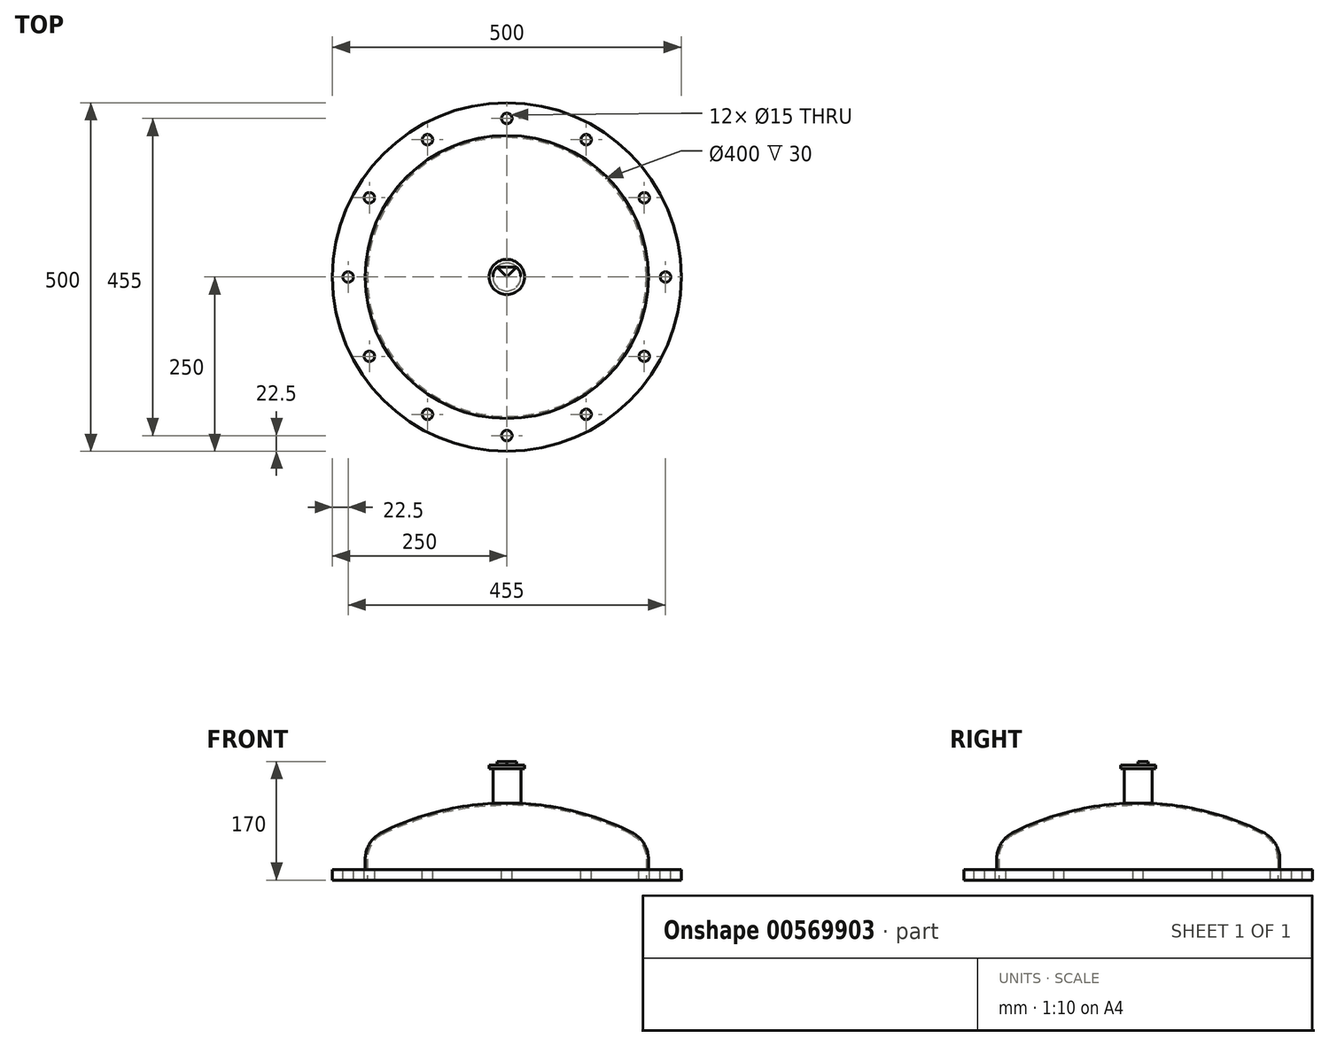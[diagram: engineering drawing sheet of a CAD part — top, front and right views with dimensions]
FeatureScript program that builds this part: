
annotation { "Feature Type Name" : "Feature", "Feature Type Description" : "" }
export const myFeature = defineFeature(function(context is Context, id is Id, definition is map)
    precondition{}
    {
        {
            var Q0;
            Q0=qCreatedBy(makeId("Front.planeOp"),FACE);
            var sketch = newSketch(context, id + "F0", { "sketchPlane" : qUnion([Q0])});
            skLineSegment(sketch, "E0", {"start": v(200, 0) * mm, "end": v(203, 0) * mm});
            skLineSegment(sketch, "E1", {"start": v(203, 0) * mm, "end": v(203, 20) * mm});
            skLineSegment(sketch, "E2", {"start": v(200, 0) * mm, "end": v(200, 20) * mm});
            skArc(sketch, "E3", {"start": v(200, 20) * mm, "mid": v(194, 41.07) * mm, "end": v(177.8, 55.82) * mm});
            skArc(sketch, "E4", {"start": v(177.8, 55.82) * mm, "mid": v(91.32, 87) * mm, "end": v(0, 97.6) * mm});
            skArc(sketch, "E5.0", {"start": v(179.13, 58.5) * mm, "mid": v(92, 89.92) * mm, "end": v(0, 100.6) * mm});
            skArc(sketch, "E5.1", {"start": v(203, 20) * mm, "mid": v(196.55, 42.65) * mm, "end": v(179.13, 58.5) * mm});
            skLineSegment(sketch, "E6", {"start": v(0, 97.6) * mm, "end": v(0, 100.6) * mm});
            skSolve(sketch);
        }
        {
            var Q0;
            Q0=qSketchRegion(id+"F0",true);
            var Q1;
            Q1=sQuery(id+"F0.wireOp",EDGE,"E6");
            revolve(context, id + "F1", {"entities" : qUnion([Q0]), "axis" : qUnion([Q1]), "revolveType" : RevolveType.FULL});
        }
        {
            var Q0;
            Q0=makeQuery(id+"F1.opRevolve","SWEPT_FACE",FACE,{"disambiguationData":[OSD([sQuery(id+"F0.wireOp",EDGE,"E0")])]});
            var sketch = newSketch(context, id + "F2", { "sketchPlane" : qUnion([Q0])});
            skCircle(sketch, "E7", {"center": v(0, 0) * mm, "radius": 250 * mm});
            skCircle(sketch, "E8", {"center": v(0, 0) * mm, "radius": 200 * mm});
            skSolve(sketch);
        }
        {
            var Q0;
            Q0=qSketchRegion(id+"F2",true);
            extrude(context, id + "F3", {"entities" : qUnion([Q0]), "operationType" : NewBodyOperationType.ADD, "depth" : 10 * mm, "offsetDistance" : 25 * mm, "hasSecondDirection" : true, "secondDirectionOppositeDirection" : true, "secondDirectionDepth" : 5 * mm});
        }
        {
            var Q0;
            Q0=makeQuery(id+"F3.opExtrude","CAP_FACE",FACE,{"disambiguationData":[OSD([sQuery(id+"F2.wireOp",EDGE,"E7"),sQuery(id+"F2.wireOp",EDGE,"E8")])],"isStart":true});
            var sketch = newSketch(context, id + "F4", { "sketchPlane" : qUnion([Q0])});
            skCircle(sketch, "E9", {"center": v(227.5, 0) * mm, "radius": 7.5 * mm});
            skCircle(sketch, "E10.1.0", {"center": v(197.02, 113.75) * mm, "radius": 7.5 * mm});
            skCircle(sketch, "E10.2.0", {"center": v(113.75, 197.02) * mm, "radius": 7.5 * mm});
            skCircle(sketch, "E10.3.0", {"center": v(0, 227.5) * mm, "radius": 7.5 * mm});
            skCircle(sketch, "E10.4.0", {"center": v(-113.75, 197.02) * mm, "radius": 7.5 * mm});
            skCircle(sketch, "E10.5.0", {"center": v(-197.02, 113.75) * mm, "radius": 7.5 * mm});
            skCircle(sketch, "E10.6.0", {"center": v(-227.5, 0) * mm, "radius": 7.5 * mm});
            skCircle(sketch, "E10.7.0", {"center": v(-197.02, -113.75) * mm, "radius": 7.5 * mm});
            skCircle(sketch, "E10.8.0", {"center": v(-113.75, -197.02) * mm, "radius": 7.5 * mm});
            skCircle(sketch, "E10.9.0", {"center": v(0, -227.5) * mm, "radius": 7.5 * mm});
            skCircle(sketch, "E10.10.0", {"center": v(113.75, -197.02) * mm, "radius": 7.5 * mm});
            skCircle(sketch, "E10.11.0", {"center": v(197.02, -113.75) * mm, "radius": 7.5 * mm});
            skPoint(sketch, "E10.center", {"position": v(0, 0) * mm});
            skSolve(sketch);
        }
        {
            var Q0;
            Q0=qSketchRegion(id+"F4",true);
            extrude(context, id + "F5", {"entities" : qUnion([Q0]), "operationType" : NewBodyOperationType.REMOVE, "endBound" : BoundingType.UP_TO_NEXT, "oppositeDirection" : true, "depth" : 25 * mm, "offsetDistance" : 25 * mm});
        }
        {
            var Q0;
            Q0=qCreatedBy(makeId("Top.planeOp"),FACE);
            cPlane(context, id + "F6", {"entities" : qUnion([Q0]), "cplaneType" : CPlaneType.OFFSET, "offset" : 150 * mm, "width" : 150 * mm, "height" : 150 * mm});
        }
        {
            var Q0;
            Q0=qCreatedBy(id+"F6.planeOp",FACE);
            var sketch = newSketch(context, id + "F7", { "sketchPlane" : qUnion([Q0])});
            skCircle(sketch, "E11", {"center": v(0, 0) * mm, "radius": 20 * mm});
            skSolve(sketch);
        }
        {
            var Q0;
            Q0 = qSketchRegion(id + "F7", true);
            extrude(context, id + "F8", {"entities" : qUnion([Q0]), "operationType" : NewBodyOperationType.ADD, "endBound" : BoundingType.UP_TO_NEXT, "oppositeDirection" : true, "depth" : 25 * mm, "offsetDistance" : 25 * mm});
        }
        {
            var Q0;
            Q0=makeQuery(id+"F8.opExtrude","CAP_FACE",FACE,{"disambiguationData":[OSD([sQuery(id+"F7.wireOp",EDGE,"E11")])],"isStart":true});
            var sketch = newSketch(context, id + "F9", { "sketchPlane" : qUnion([Q0])});
            skCircle(sketch, "E12", {"center": v(0, 0) * mm, "radius": 25.25 * mm});
            skSolve(sketch);
        }
        {
            var Q0;
            Q0 = qSketchRegion(id + "F9", true);
            extrude(context, id + "F10", {"entities" : qUnion([Q0]), "operationType" : NewBodyOperationType.ADD, "depth" : 5 * mm, "offsetDistance" : 25 * mm});
        }
        {
            var Q0;
            Q0=makeQuery(id+"F10.opExtrude","CAP_FACE",FACE,{"disambiguationData":[OSD([sQuery(id+"F9.wireOp",EDGE,"E12")])],"isStart":false});
            var sketch = newSketch(context, id + "F11", { "sketchPlane" : qUnion([Q0])});
            skLineSegment(sketch, "E13", {"start": v(0, 0) * mm, "end": v(14.14, 14.14) * mm});
            skLineSegment(sketch, "E14", {"start": v(0, 0) * mm, "end": v(-14.14, 14.14) * mm});
            skLineSegment(sketch, "E15", {"start": v(0, 0) * mm, "end": v(12, 0) * mm, "construction": true});
            skLineSegment(sketch, "E16", {"start": v(-14.14, 14.14) * mm, "end": v(14.14, 14.14) * mm});
            skSolve(sketch);
        }
        {
            var Q0;
            Q0 = qSketchRegion(id + "F11", true);
            extrude(context, id + "F12", {"entities" : qUnion([Q0]), "operationType" : NewBodyOperationType.ADD, "depth" : 5 * mm, "offsetDistance" : 25 * mm});
        }
    });
